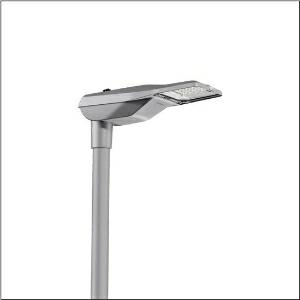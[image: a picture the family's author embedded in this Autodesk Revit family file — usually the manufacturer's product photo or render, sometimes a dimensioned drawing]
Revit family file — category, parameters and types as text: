
# Revit family: streetlight_sl_21_iq_micro___p0_8a_5xe1u31v08db_560e
name_source: partatom
category: Lighting Fixtures
units: mm (PartAtom-declared; Revit-internal decimal feet)

## family parameters
Cut with Voids When Loaded = No
Host = Face
Light Source = No
Part Type = Normal
Room Calculation Point = No
Round Connector Dimension = Use Diameter
Shared = No

## types (1)
- --- (1 x LED, 5130 lm, 39.1 W, 3000K)
    Apparent Load = 39 VA
    CIE Flux Codes = 33 69 96 100 100
    Color Rendering = 70
    Color Temperature = 3000K
    Default Elevation = 1800 mm
    Description = Streetlight SL 21 iQ micro, mast luminaire, primary light control with lens, of PMMA, primary optical cover: cover, of toughened safety glass, transparent, light distribution: P0.8a, light emission: direct distribution, primary light characteristic: asymmetric, installation type: post-top, side-entry, LED, High Power LED, rated luminous flux: 5.130lm, luminous efficacy: 131lm/W, light colour: 730, colour temperature: 3000K, control gear: iQ-Street Remote, D4i with power reduction, control: pre-setting: logarithmic dimming characteristic, Street-Remote, Auto-Match, Temp-Guard, Lumen-Switch, Night-Set, Smart-Wire, Light-Fading, Desk-Remote (wireless, voltage-free reading and setting of iQ features in the workshop via application-optimized NFC function/RFID function), optimised constant luminous flux control (CLO 2.0), mains connection: 220..240V, AC, 50/60Hz, start of lifetime: 39W, end of service life: 41W, reduction: 17W, luminaire housing, of diecast aluminium, powder-coated, Siteco® metallic grey (DB 702S), corrosivity category C5 mid according to DIN EN ISO 12944, please order mast flange separately, inclination adjustable: 0°, 5°, 10°, 15°, sealing non-destructively replaceable, multi-level sealing system, length: 528mm, width: 235mm, height: 110mm, mast flange for spigot size: 42mm (side-entry): 5XC10008XM4, 60/48mm (side-entry/post-top): 5XC10108XM2, 76/60mm (side-entry/post-top): 5XC10108XM1, mounting height: 4..8m, Smart Interface above, protection rating (complete): IP66, insulation class (complete): insulation class II (safety insulation), certification: CE, ENEC, ENEC+, VDE, impact resistance: IK10, permissible operating ambient temperature for outdoor applications: -40..+50°C, standard-compliant lighting for roads and squares, packaging unit: 1 piece

Light Distribution: P0.8a
    Height = 110 mm
    Lamp = 1 x LED
    Lamp Light Flux = 5130 lm
    Lamp Power = 39.1 W
    Lamp count = 1
    Length = 528 mm
    Luminous efficacy = 131 lm/W
    Manufacturer = Siteco
    ModVariant = No
    Model = 5XE1U31V08DB
    Number of Poles = 1
    OnlyDefault = Yes
    Power Factor = 1
    Product Name = Streetlight SL 21 iQ micro | P0.8a
    Product group = mast luminaire | pylon top
    ProductGroupID = 6100
    Protection Class = Protection class II
    Protection Degree = IP 66
    RLX_Detail_Level = 1
    RLX_Emergency_Light_Flux = 0 lm
    RLX_Emergency_Type = 0
    RLX_Emergency_Type_DB = No
    RlxData = <blob elided: 99233 chars, md5=9d8c7579>
    Socket = socket
    Standby Power = 0 W
    System Light Flux = 5130 lm
    System Power = 39 W
    Type Comments = factory setting: luminous flux: 100 % | dim-lin: 254 | 765 mA
    Type Image = l_1277292.jpg
    URL = http://relux.com
    VarID = @adj_095817
    Voltage = 0 V
    Weight = 0.00 kg
    Width = 235 mm

## geometry (parser evidence)
native form markers: Blend x4, Sweep x10
no freeform markers — native parametric forms only
